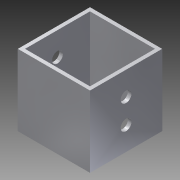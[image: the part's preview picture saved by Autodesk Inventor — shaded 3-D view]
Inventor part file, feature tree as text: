
AUTODESK INVENTOR PART (.ipt)
format: ipt  version: 2015 (Build 190159000, 159)  size: 117,760 bytes
history: native  units: mm
features: sketch x2, other x1, extrude x1, hole x1
ambient origin geometry x8: Origin, YZ Plane, XZ Plane, XY Plane, X Axis, Y Axis, Z Axis, Center Point
bodies: Body1 (feature_tree)
feature tree (5):
  other  "ソリッド1"
  extrude  "押し出し1"  Depth=36.0mm
  hole  "穴1"  [1 undecoded]
  sketch  "スケッチ1"
  sketch  "スケッチ2"
note: 1 required parameter value undecoded (feature->parameter linkage not recoverable at this tier; creation-order binding heuristic only, values carry confidence <= 0.55)
